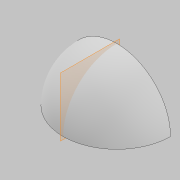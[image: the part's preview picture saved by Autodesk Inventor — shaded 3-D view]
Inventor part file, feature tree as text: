
AUTODESK INVENTOR PART (.ipt)
format: ipt  version: 2021 (Build 250183000, 183)  size: 119,808 bytes
history: native  units: mm
features: other x3, revolve x1, sketch x1
ambient origin geometry x8: Origin, YZ Plane, XZ Plane, XY Plane, X Axis, Y Axis, Z Axis, Center Point
bodies: Body1 (feature_tree)
feature tree (5):
  revolve  "Revolution1"  [1 undecoded]
  other  "midPlane"
  sketch  "Sketch1"  dims[d0=10.0mm d1=890.0mm d2=0.0mm d3=0.0mm d6=180.0deg d7=900.0mm d8=-900.0mm]
  other  "tangent1"
  other  "tangent2"
note: 1 required parameter value undecoded (feature->parameter linkage not recoverable at this tier; creation-order binding heuristic only, values carry confidence <= 0.55)
